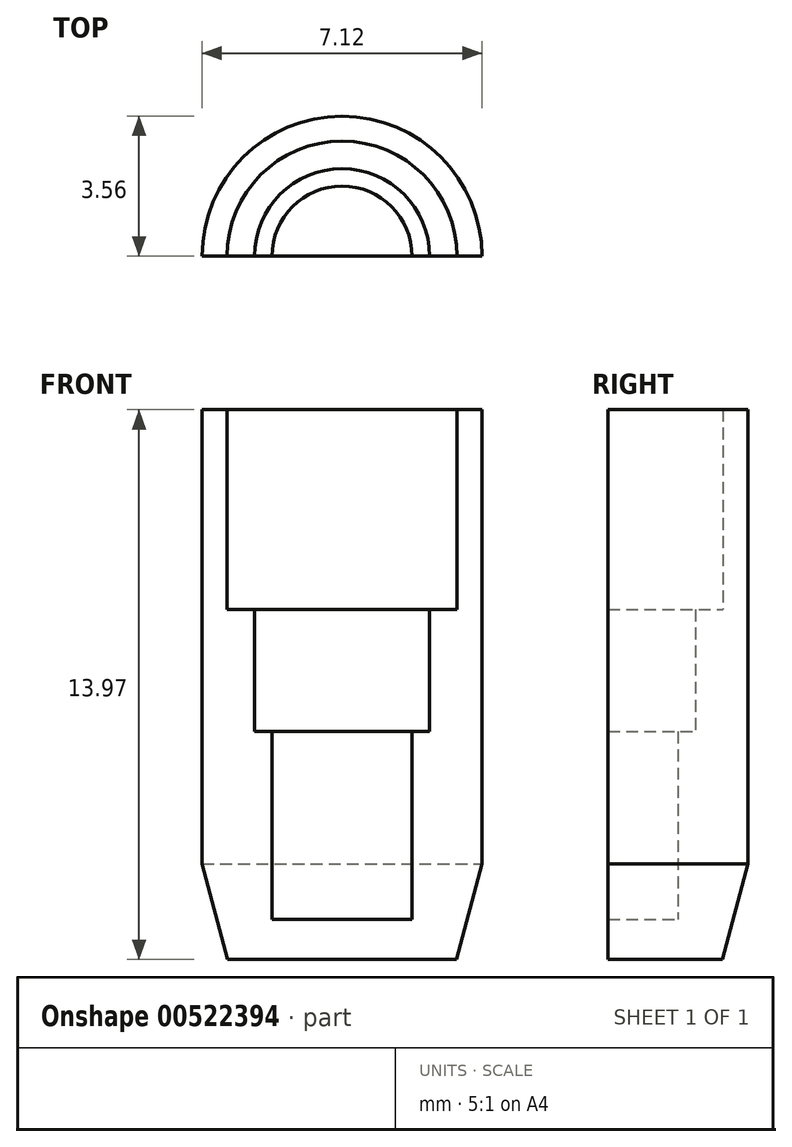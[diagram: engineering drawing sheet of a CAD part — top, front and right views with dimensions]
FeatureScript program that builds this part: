
annotation { "Feature Type Name" : "Feature", "Feature Type Description" : "" }
export const myFeature = defineFeature(function(context is Context, id is Id, definition is map)
    precondition{}
    {
        {
            var Q0;
            Q0=qCreatedBy(makeId("Front.planeOp"),FACE);
            var sketch = newSketch(context, id + "F0", { "sketchPlane" : qUnion([Q0])});
            skLineSegment(sketch, "E0", {"start": v(3.56, 2.43) * mm, "end": v(2.9, 0) * mm});
            skLineSegment(sketch, "E1", {"start": v(2.9, 0) * mm, "end": v(0, 0) * mm});
            skLineSegment(sketch, "E2", {"start": v(0, 0) * mm, "end": v(0, 1.02) * mm});
            skLineSegment(sketch, "E3", {"start": v(0, 1.02) * mm, "end": v(1.78, 1.02) * mm});
            skLineSegment(sketch, "E4", {"start": v(1.78, 1.02) * mm, "end": v(1.78, 5.8) * mm});
            skLineSegment(sketch, "E5", {"start": v(1.78, 5.8) * mm, "end": v(2.22, 5.8) * mm});
            skLineSegment(sketch, "E6", {"start": v(2.22, 5.8) * mm, "end": v(2.22, 8.9) * mm});
            skLineSegment(sketch, "E7", {"start": v(2.92, 13.97) * mm, "end": v(3.56, 13.97) * mm});
            skLineSegment(sketch, "E8", {"start": v(3.56, 2.43) * mm, "end": v(3.56, 13.97) * mm});
            skLineSegment(sketch, "E9", {"start": v(2.92, 13.97) * mm, "end": v(2.92, 8.9) * mm});
            skLineSegment(sketch, "E10", {"start": v(2.92, 8.9) * mm, "end": v(2.22, 8.9) * mm});
            skSolve(sketch);
        }
        {
            var Q0;
            Q0=qSketchRegion(id+"F0",true);
            var Q1;
            Q1=sQuery(id+"F0.wireOp",EDGE,"E2");
            revolve(context, id + "F1", {"entities" : qUnion([Q0]), "axis" : qUnion([Q1]), "revolveType" : RevolveType.ONE_DIRECTION, "angle" : 180 * degree});
        }
    });
